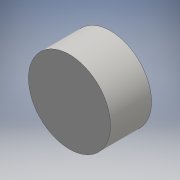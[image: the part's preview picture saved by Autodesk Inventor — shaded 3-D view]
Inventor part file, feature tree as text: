
AUTODESK INVENTOR PART (.ipt)
format: ipt  version: 2016 (Build 200138000, 138)  size: 92,672 bytes
history: native  units: mm
features: sketch x2, extrude x1
ambient origin geometry x8: Origin, YZ Plane, XZ Plane, XY Plane, X Axis, Y Axis, Z Axis, Center Point
bodies: Solid1 (feature_tree)
feature tree (3):
  extrude  "Extrusion1"  Depth=10.0mm TaperAngle=0.0deg
  sketch  "Sketch2"  dims[d3=6.981317mm d4=5.0mm d5=8.0mm]
  sketch  "Sketch1"  dims[d0=20.0mm d1=10.0mm d2=0.0mm]
